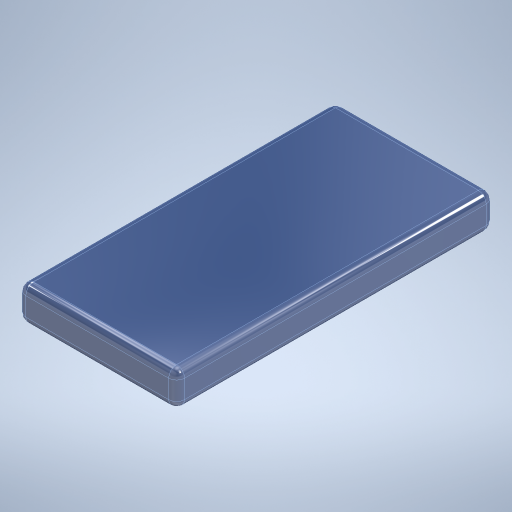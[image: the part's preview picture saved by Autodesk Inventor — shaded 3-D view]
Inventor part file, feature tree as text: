
AUTODESK INVENTOR PART (.ipt)
format: ipt  version: 2023 (Build 270158000, 158)  size: 257,536 bytes
history: native  units: in
note: dims shown in document units (in); Inventor stores cm internally (conversion verified against a paired STEP export)
features: extrude x1, fillet x1, sketch x1
ambient origin geometry x8: Origin, YZ Plane, XZ Plane, XY Plane, X Axis, Y Axis, Z Axis, Center Point
bodies: Solid1 (feature_tree)
feature tree (3):
  extrude  "Extrusion1"  Depth=4.7244in
  fillet  "Fillet1"  Radius=0.5118in
  sketch  "Sketch1"  dims[d0=2.3622in d1=4.7244in d2=0.5118in d3=0.0in d4=0.1181in d5=0.0in d6=0.0in d7=0.0in]
